# Revit family: SANINDUSA_118610_SlopHopper410x505x435_V0
name_source: partatom
category: Plumbing Fixtures
units: mm (PartAtom-declared; Revit-internal decimal feet)

## family parameters
Cut with Voids When Loaded = No
Host = Face
Part Type = Normal
Room Calculation Point = No
Round Connector Dimension = Use Diameter
Shared = No

## types (1)
- SANINDUSA_118610_SlopHopper410x505x435_V0
    AssetType = Fixed
    CodePerformance = EN 997:2012+A1:2015 CL 1 - 7 A
    Color = white
    Constituents = Compatible with fixing kit ref. 400 (not included). Grid for slop hopper ref. 4A1861  (not included). Eco horizontal exterior flow meter 3/4" ref. 5190841 (not included).
    Default Elevation = 1219 mm
    Description = Soil appliance for the disposal of waste
    DrainSize = 100 mm  [stored 0.328084 ft]
    Features = slop hoppers are designed for use in hospitals, nursing homes, and GP surgeries to enable the safe and hygienic disposal of clinical waste, such as the contents of vomit bowls, drainage bags, bedpans, and urine bottles. They can also be used in a domestic setting for individuals with chronic health conditions.
    Finish = gloss
    InletDiameter = 0 mm  [stored 0 ft]
    Installation Instructions = https://www.tec.sanindusa.pt
    Manufacturer = Sanindusa
    ManufacturerName = Sanindusa
    ManufacturerURL = www.tec.sanindusa.pt
    Material = vitreous china
    Model = 118610
    ModelNumber = 118610
    Name = Slop hopper
    NominalHeight = 435 mm  [stored 1.42717 ft]
    NominalLength = 410 mm  [stored 1.34514 ft]
    NominalWidth = 505 mm  [stored 1.65682 ft]
    ProductInformation = https://www.tec.sanindusa.pt
    ProductionYear = 2004
    Size = 410x505x435
    ToiletPanType = washdown
    ToiletType = LooseCoupled
    Type (IFC) = IfcSanitaryTerminalType
    URL = www.tec.sanindusa.pt
    Version = 1
    WarrantyDescription = https://www.tec.sanindusa.pt
    WarrantyDurationParts = 5
    WarrantyDurationUnit = year
    WashHandBasinMounting = pedestal
    WashHandBasinType = LooseCoupled
    Waste Connection = Yes
    Weight = 21.00 kg

note: [stored X ft] marks values corroborated as IEEE doubles in the binary element streams (Revit-internal decimal feet)

## geometry (parser evidence)
native form markers: Sweep x8
no freeform markers — native parametric forms only
